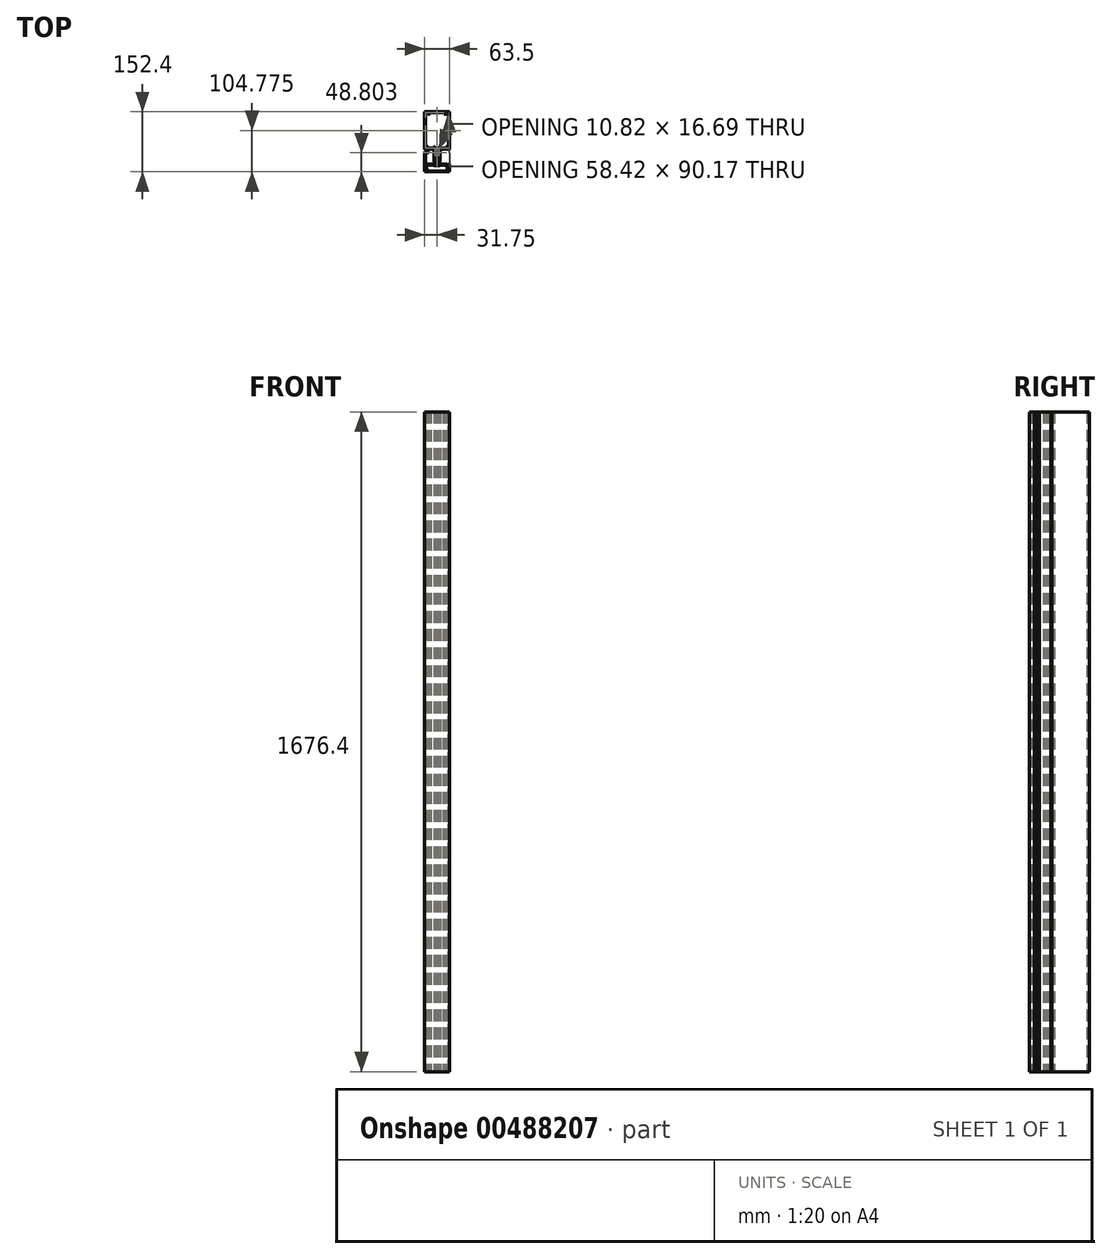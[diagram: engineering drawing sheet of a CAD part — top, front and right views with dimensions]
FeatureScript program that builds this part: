
annotation { "Feature Type Name" : "Feature", "Feature Type Description" : "" }
export const myFeature = defineFeature(function(context is Context, id is Id, definition is map)
    precondition{}
    {
        {
            var Q0;
            Q0=qCreatedBy(makeId("Top.planeOp"),FACE);
            var sketch = newSketch(context, id + "F0", { "sketchPlane" : qUnion([Q0])});
            skLineSegment(sketch, "E0", {"start": v(54.45, -82.55) * mm, "end": v(54.45, -2.69) * mm});
            skLineSegment(sketch, "E1", {"start": v(54.45, -2.69) * mm, "end": v(49.06, -1.35) * mm});
            skLineSegment(sketch, "E2", {"start": v(49.06, -1.35) * mm, "end": v(59.85, 1.35) * mm});
            skLineSegment(sketch, "E3", {"start": v(59.85, 1.35) * mm, "end": v(54.46, 2.69) * mm});
            skLineSegment(sketch, "E4", {"start": v(54.46, 2.69) * mm, "end": v(54.45, 82.55) * mm});
            skLineSegment(sketch, "E5", {"start": v(54.45, -31.75) * mm, "end": v(-9.05, -31.75) * mm});
            skLineSegment(sketch, "E6", {"start": v(-9.05, -44.45) * mm, "end": v(54.45, -44.45) * mm});
            skLineSegment(sketch, "E7", {"start": v(-2.7, -31.75) * mm, "end": v(-2.7, -44.45) * mm});
            skLineSegment(sketch, "E8", {"start": v(3.65, -76.2) * mm, "end": v(54.45, -76.2) * mm});
            skLineSegment(sketch, "E9", {"start": v(4.74, -64.5) * mm, "end": v(54.45, -64.5) * mm});
            skLineSegment(sketch, "E10", {"start": v(4.74, -11.7) * mm, "end": v(54.45, -11.7) * mm});
            skLineSegment(sketch, "E11", {"start": v(3.65, 76.2) * mm, "end": v(54.45, 76.2) * mm});
            skLineSegment(sketch, "E12", {"start": v(54.45, -25.4) * mm, "end": v(-9.05, -25.4) * mm});
            skLineSegment(sketch, "E13", {"start": v(-9.05, -25.4) * mm, "end": v(-9.05, -50.8) * mm});
            skLineSegment(sketch, "E14", {"start": v(-9.05, -50.8) * mm, "end": v(54.45, -50.8) * mm});
            skLineSegment(sketch, "E15", {"start": v(-24.72, -57.15) * mm, "end": v(-24.72, -60.33) * mm});
            skLineSegment(sketch, "E16", {"start": v(-31.48, -57.15) * mm, "end": v(-31.48, -60.33) * mm});
            skLineSegment(sketch, "E17", {"start": v(-50.7, -19.04) * mm, "end": v(-50.7, -25.4) * mm});
            skLineSegment(sketch, "E18", {"start": v(-59.84, -25.4) * mm, "end": v(-59.84, -19.04) * mm});
            skLineSegment(sketch, "E19", {"start": v(-36.05, -50.8) * mm, "end": v(-34.46, -50.8) * mm});
            skLineSegment(sketch, "E20", {"start": v(-36.05, -57.15) * mm, "end": v(-36.05, -50.8) * mm});
            skLineSegment(sketch, "E21", {"start": v(-20.15, -50.8) * mm, "end": v(-20.15, -57.15) * mm});
            skLineSegment(sketch, "E22", {"start": v(-21.74, -50.8) * mm, "end": v(-20.15, -50.8) * mm});
            skLineSegment(sketch, "E23", {"start": v(-36.05, -57.15) * mm, "end": v(-34.46, -57.15) * mm});
            skLineSegment(sketch, "E24", {"start": v(-21.74, -57.15) * mm, "end": v(-20.15, -57.15) * mm});
            skLineSegment(sketch, "E25", {"start": v(-34.45, -60.33) * mm, "end": v(-21.75, -60.33) * mm});
            skLineSegment(sketch, "E26", {"start": v(-58.58, -74.68) * mm, "end": v(-58.58, -65.43) * mm});
            skLineSegment(sketch, "E27", {"start": v(-58.58, -65.43) * mm, "end": v(-57.82, -65.43) * mm});
            skArc(sketch, "E28", {"start": v(-57.82, -65.43) * mm, "mid": v(-56.8, -64.41) * mm, "end": v(-57.82, -63.4) * mm});
            skLineSegment(sketch, "E29", {"start": v(-57.82, -63.4) * mm, "end": v(-58.33, -63.4) * mm});
            skArc(sketch, "E30", {"start": v(-58.33, -63.4) * mm, "mid": v(-59.4, -63.84) * mm, "end": v(-59.85, -64.92) * mm});
            skLineSegment(sketch, "E31", {"start": v(-59.85, -64.92) * mm, "end": v(-59.85, -76.2) * mm});
            skLineSegment(sketch, "E32", {"start": v(-59.85, -76.2) * mm, "end": v(3.65, -76.2) * mm});
            skLineSegment(sketch, "E33", {"start": v(3.65, -76.2) * mm, "end": v(3.65, -64.92) * mm});
            skArc(sketch, "E34", {"start": v(3.65, -64.92) * mm, "mid": v(3.2, -63.84) * mm, "end": v(2.13, -63.4) * mm});
            skLineSegment(sketch, "E35", {"start": v(2.13, -63.4) * mm, "end": v(1.62, -63.4) * mm});
            skArc(sketch, "E36", {"start": v(1.62, -63.4) * mm, "mid": v(0.6, -64.41) * mm, "end": v(1.62, -65.43) * mm});
            skLineSegment(sketch, "E37", {"start": v(1.62, -65.43) * mm, "end": v(2.38, -65.43) * mm});
            skLineSegment(sketch, "E38", {"start": v(2.38, -65.43) * mm, "end": v(2.38, -74.68) * mm});
            skLineSegment(sketch, "E39", {"start": v(2.38, -74.68) * mm, "end": v(-58.58, -74.68) * mm});
            skLineSegment(sketch, "E40", {"start": v(-8.53, -57.14) * mm, "end": v(-8.53, -50.8) * mm});
            skLineSegment(sketch, "E41", {"start": v(7.13, -50.8) * mm, "end": v(5.18, -64.5) * mm});
            skLineSegment(sketch, "E42", {"start": v(5.18, -64.5) * mm, "end": v(3.66, -64.5) * mm});
            skLineSegment(sketch, "E43", {"start": v(3.66, -64.5) * mm, "end": v(3.66, -61.57) * mm});
            skLineSegment(sketch, "E44", {"start": v(-8.53, -19.06) * mm, "end": v(-8.53, -25.4) * mm});
            skLineSegment(sketch, "E45", {"start": v(7.13, -25.4) * mm, "end": v(5.18, -11.7) * mm});
            skLineSegment(sketch, "E46", {"start": v(5.18, -11.7) * mm, "end": v(3.66, -11.7) * mm});
            skLineSegment(sketch, "E47", {"start": v(3.66, -11.7) * mm, "end": v(3.66, -14.63) * mm});
            skLineSegment(sketch, "E48", {"start": v(-33.5, -23.22) * mm, "end": v(-33.5, -34.99) * mm});
            skArc(sketch, "E49", {"start": v(-33.5, -34.99) * mm, "mid": v(-32.85, -35.74) * mm, "end": v(-32.01, -35.19) * mm});
            skLineSegment(sketch, "E50", {"start": v(-32.01, -35.19) * mm, "end": v(-31.6, -33.68) * mm});
            skArc(sketch, "E51", {"start": v(-31.6, -33.68) * mm, "mid": v(-28.1, -30.99) * mm, "end": v(-24.6, -33.68) * mm});
            skLineSegment(sketch, "E52", {"start": v(-24.6, -33.68) * mm, "end": v(-24.19, -35.19) * mm});
            skArc(sketch, "E53", {"start": v(-24.19, -35.19) * mm, "mid": v(-23.35, -35.74) * mm, "end": v(-22.69, -34.99) * mm});
            skLineSegment(sketch, "E54", {"start": v(-22.69, -34.99) * mm, "end": v(-22.69, -23.22) * mm});
            skArc(sketch, "E55", {"start": v(-22.69, -23.22) * mm, "mid": v(-23.8, -22.19) * mm, "end": v(-24.21, -20.73) * mm});
            skLineSegment(sketch, "E56", {"start": v(-24.21, -20.73) * mm, "end": v(-24.21, -19.05) * mm});
            skLineSegment(sketch, "E57", {"start": v(-24.21, -19.05) * mm, "end": v(-31.99, -19.05) * mm});
            skLineSegment(sketch, "E58", {"start": v(-31.99, -19.05) * mm, "end": v(-31.99, -20.73) * mm});
            skArc(sketch, "E59", {"start": v(-31.99, -20.73) * mm, "mid": v(-32.4, -22.19) * mm, "end": v(-33.5, -23.22) * mm});
            skLineSegment(sketch, "E60", {"start": v(-43.6, -19.05) * mm, "end": v(-34.78, -19.05) * mm});
            skArc(sketch, "E61", {"start": v(-34.78, -19.05) * mm, "mid": v(-34.6, -19.12) * mm, "end": v(-34.53, -19.3) * mm});
            skLineSegment(sketch, "E62", {"start": v(-34.53, -19.3) * mm, "end": v(-34.53, -20.73) * mm});
            skArc(sketch, "E63", {"start": v(-34.53, -20.73) * mm, "mid": v(-34.6, -20.9) * mm, "end": v(-34.78, -20.98) * mm});
            skLineSegment(sketch, "E64", {"start": v(-34.78, -20.98) * mm, "end": v(-35.8, -20.98) * mm});
            skArc(sketch, "E65", {"start": v(-35.8, -20.98) * mm, "mid": v(-35.98, -21.05) * mm, "end": v(-36.05, -21.23) * mm});
            skLineSegment(sketch, "E66", {"start": v(-36.05, -21.23) * mm, "end": v(-36.05, -50.8) * mm});
            skLineSegment(sketch, "E67", {"start": v(-36.05, -50.8) * mm, "end": v(-35.03, -50.8) * mm});
            skLineSegment(sketch, "E68", {"start": v(-35.03, -50.8) * mm, "end": v(-34.65, -51.18) * mm});
            skLineSegment(sketch, "E69", {"start": v(-34.65, -51.18) * mm, "end": v(-34.27, -50.8) * mm});
            skLineSegment(sketch, "E70", {"start": v(-34.27, -50.8) * mm, "end": v(-32.42, -50.8) * mm});
            skLineSegment(sketch, "E71", {"start": v(-32.42, -50.8) * mm, "end": v(-32.04, -51.18) * mm});
            skLineSegment(sketch, "E72", {"start": v(-32.04, -51.18) * mm, "end": v(-31.66, -50.8) * mm});
            skLineSegment(sketch, "E73", {"start": v(-31.66, -50.8) * mm, "end": v(-30.64, -50.8) * mm});
            skLineSegment(sketch, "E74", {"start": v(-30.64, -50.8) * mm, "end": v(-30.64, -39.88) * mm});
            skLineSegment(sketch, "E75", {"start": v(-30.64, -39.88) * mm, "end": v(-29.16, -34.34) * mm});
            skArc(sketch, "E76", {"start": v(-29.16, -34.34) * mm, "mid": v(-28.1, -33.53) * mm, "end": v(-27.04, -34.34) * mm});
            skLineSegment(sketch, "E77", {"start": v(-27.04, -34.34) * mm, "end": v(-25.56, -39.88) * mm});
            skLineSegment(sketch, "E78", {"start": v(-25.56, -39.88) * mm, "end": v(-25.56, -50.8) * mm});
            skLineSegment(sketch, "E79", {"start": v(-25.56, -50.8) * mm, "end": v(-24.54, -50.8) * mm});
            skLineSegment(sketch, "E80", {"start": v(-24.54, -50.8) * mm, "end": v(-24.16, -51.18) * mm});
            skLineSegment(sketch, "E81", {"start": v(-24.16, -51.18) * mm, "end": v(-23.78, -50.8) * mm});
            skLineSegment(sketch, "E82", {"start": v(-23.78, -50.8) * mm, "end": v(-21.93, -50.8) * mm});
            skLineSegment(sketch, "E83", {"start": v(-21.93, -50.8) * mm, "end": v(-21.55, -51.18) * mm});
            skLineSegment(sketch, "E84", {"start": v(-21.55, -51.18) * mm, "end": v(-21.17, -50.8) * mm});
            skLineSegment(sketch, "E85", {"start": v(-21.17, -50.8) * mm, "end": v(-20.15, -50.8) * mm});
            skLineSegment(sketch, "E86", {"start": v(-20.15, -50.8) * mm, "end": v(-20.15, -21.23) * mm});
            skArc(sketch, "E87", {"start": v(-20.15, -21.23) * mm, "mid": v(-20.22, -21.05) * mm, "end": v(-20.4, -20.98) * mm});
            skLineSegment(sketch, "E88", {"start": v(-20.4, -20.98) * mm, "end": v(-21.42, -20.98) * mm});
            skArc(sketch, "E89", {"start": v(-21.42, -20.98) * mm, "mid": v(-21.6, -20.9) * mm, "end": v(-21.67, -20.73) * mm});
            skLineSegment(sketch, "E90", {"start": v(-21.67, -20.73) * mm, "end": v(-21.67, -19.3) * mm});
            skArc(sketch, "E91", {"start": v(-21.67, -19.3) * mm, "mid": v(-21.6, -19.12) * mm, "end": v(-21.42, -19.05) * mm});
            skLineSegment(sketch, "E92", {"start": v(-21.42, -19.05) * mm, "end": v(-12.6, -19.05) * mm});
            skLineSegment(sketch, "E93", {"start": v(-12.6, -19.05) * mm, "end": v(-12.22, -18.67) * mm});
            skLineSegment(sketch, "E94", {"start": v(-12.22, -18.67) * mm, "end": v(-11.84, -19.05) * mm});
            skLineSegment(sketch, "E95", {"start": v(-11.84, -19.05) * mm, "end": v(-2.9, -19.05) * mm});
            skArc(sketch, "E96", {"start": v(-2.9, -19.05) * mm, "mid": v(-2.55, -18.81) * mm, "end": v(-2.63, -18.4) * mm});
            skArc(sketch, "E97", {"start": v(-2.63, -18.4) * mm, "mid": v(-3.13, -17.66) * mm, "end": v(-3.3, -16.78) * mm});
            skLineSegment(sketch, "E98", {"start": v(-3.3, -16.78) * mm, "end": v(-3.3, -16.51) * mm});
            skArc(sketch, "E99", {"start": v(-3.3, -16.51) * mm, "mid": v(-2.94, -15.61) * mm, "end": v(-2.04, -15.24) * mm});
            skLineSegment(sketch, "E100", {"start": v(-2.04, -15.24) * mm, "end": v(0.2, -15.24) * mm});
            skArc(sketch, "E101", {"start": v(0.2, -15.24) * mm, "mid": v(1.1, -15.61) * mm, "end": v(1.47, -16.51) * mm});
            skLineSegment(sketch, "E102", {"start": v(1.47, -16.51) * mm, "end": v(1.47, -16.78) * mm});
            skArc(sketch, "E103", {"start": v(1.47, -16.78) * mm, "mid": v(1.3, -17.66) * mm, "end": v(0.8, -18.4) * mm});
            skArc(sketch, "E104", {"start": v(0.8, -18.4) * mm, "mid": v(0.7, -18.81) * mm, "end": v(1.06, -19.05) * mm});
            skLineSegment(sketch, "E105", {"start": v(1.06, -19.05) * mm, "end": v(3.14, -19.05) * mm});
            skArc(sketch, "E106", {"start": v(3.14, -19.05) * mm, "mid": v(3.5, -18.9) * mm, "end": v(3.65, -18.54) * mm});
            skLineSegment(sketch, "E107", {"start": v(3.65, -18.54) * mm, "end": v(3.65, 76.2) * mm});
            skLineSegment(sketch, "E108", {"start": v(3.65, 76.2) * mm, "end": v(-59.85, 76.2) * mm});
            skLineSegment(sketch, "E109", {"start": v(-59.85, 76.2) * mm, "end": v(-59.85, -18.54) * mm});
            skArc(sketch, "E110", {"start": v(-59.85, -18.54) * mm, "mid": v(-59.7, -18.9) * mm, "end": v(-59.34, -19.05) * mm});
            skLineSegment(sketch, "E111", {"start": v(-59.34, -19.05) * mm, "end": v(-57.26, -19.05) * mm});
            skArc(sketch, "E112", {"start": v(-57.26, -19.05) * mm, "mid": v(-56.9, -18.81) * mm, "end": v(-57, -18.4) * mm});
            skArc(sketch, "E113", {"start": v(-57, -18.4) * mm, "mid": v(-57.49, -17.66) * mm, "end": v(-57.67, -16.78) * mm});
            skLineSegment(sketch, "E114", {"start": v(-57.67, -16.78) * mm, "end": v(-57.67, -16.51) * mm});
            skArc(sketch, "E115", {"start": v(-57.67, -16.51) * mm, "mid": v(-57.3, -15.61) * mm, "end": v(-56.4, -15.24) * mm});
            skLineSegment(sketch, "E116", {"start": v(-56.4, -15.24) * mm, "end": v(-54.16, -15.24) * mm});
            skArc(sketch, "E117", {"start": v(-54.16, -15.24) * mm, "mid": v(-53.26, -15.61) * mm, "end": v(-52.9, -16.51) * mm});
            skLineSegment(sketch, "E118", {"start": v(-52.9, -16.51) * mm, "end": v(-52.9, -16.78) * mm});
            skArc(sketch, "E119", {"start": v(-52.9, -16.78) * mm, "mid": v(-53.07, -17.66) * mm, "end": v(-53.56, -18.4) * mm});
            skArc(sketch, "E120", {"start": v(-53.56, -18.4) * mm, "mid": v(-53.65, -18.81) * mm, "end": v(-53.3, -19.05) * mm});
            skLineSegment(sketch, "E121", {"start": v(-53.3, -19.05) * mm, "end": v(-44.36, -19.05) * mm});
            skLineSegment(sketch, "E122", {"start": v(-44.36, -19.05) * mm, "end": v(-43.97, -18.67) * mm});
            skLineSegment(sketch, "E123", {"start": v(-43.97, -18.67) * mm, "end": v(-43.6, -19.05) * mm});
            skArc(sketch, "E124", {"start": v(-34.02, -13.2) * mm, "mid": v(-34.17, -12.85) * mm, "end": v(-34.53, -12.7) * mm});
            skLineSegment(sketch, "E125", {"start": v(-34.53, -12.7) * mm, "end": v(-35.54, -12.7) * mm});
            skArc(sketch, "E126", {"start": v(-35.54, -12.7) * mm, "mid": v(-35.9, -12.85) * mm, "end": v(-36.05, -13.2) * mm});
            skLineSegment(sketch, "E127", {"start": v(-36.05, -13.2) * mm, "end": v(-36.05, -15.88) * mm});
            skLineSegment(sketch, "E128", {"start": v(-36.05, -15.88) * mm, "end": v(-50.83, -15.88) * mm});
            skLineSegment(sketch, "E129", {"start": v(-50.83, -15.88) * mm, "end": v(-50.83, -13.2) * mm});
            skArc(sketch, "E130", {"start": v(-50.83, -13.2) * mm, "mid": v(-50.98, -12.85) * mm, "end": v(-51.34, -12.7) * mm});
            skLineSegment(sketch, "E131", {"start": v(-51.34, -12.7) * mm, "end": v(-56.55, -12.7) * mm});
            skArc(sketch, "E132", {"start": v(-56.55, -12.7) * mm, "mid": v(-57.09, -12.48) * mm, "end": v(-57.3, -11.94) * mm});
            skLineSegment(sketch, "E133", {"start": v(-57.3, -11.94) * mm, "end": v(-57.3, 73.66) * mm});
            skLineSegment(sketch, "E134", {"start": v(-57.3, 73.66) * mm, "end": v(-53.25, 73.66) * mm});
            skArc(sketch, "E135", {"start": v(-53.25, 73.66) * mm, "mid": v(-52.17, 73.21) * mm, "end": v(-51.72, 72.14) * mm});
            skLineSegment(sketch, "E136", {"start": v(-51.72, 72.14) * mm, "end": v(-51.72, 70.61) * mm});
            skLineSegment(sketch, "E137", {"start": v(-51.72, 70.61) * mm, "end": v(-45.75, 70.61) * mm});
            skLineSegment(sketch, "E138", {"start": v(-45.75, 70.61) * mm, "end": v(-45.75, 72.14) * mm});
            skArc(sketch, "E139", {"start": v(-45.75, 72.14) * mm, "mid": v(-45.3, 73.21) * mm, "end": v(-44.23, 73.66) * mm});
            skLineSegment(sketch, "E140", {"start": v(-44.23, 73.66) * mm, "end": v(-11.97, 73.66) * mm});
            skArc(sketch, "E141", {"start": v(-11.97, 73.66) * mm, "mid": v(-10.9, 73.21) * mm, "end": v(-10.45, 72.14) * mm});
            skLineSegment(sketch, "E142", {"start": v(-10.45, 72.14) * mm, "end": v(-10.45, 70.61) * mm});
            skLineSegment(sketch, "E143", {"start": v(-10.45, 70.61) * mm, "end": v(-4.48, 70.61) * mm});
            skLineSegment(sketch, "E144", {"start": v(-4.48, 70.61) * mm, "end": v(-4.48, 72.14) * mm});
            skArc(sketch, "E145", {"start": v(-4.48, 72.14) * mm, "mid": v(-4.03, 73.21) * mm, "end": v(-2.95, 73.66) * mm});
            skLineSegment(sketch, "E146", {"start": v(-2.95, 73.66) * mm, "end": v(1.11, 73.66) * mm});
            skLineSegment(sketch, "E147", {"start": v(1.11, 73.66) * mm, "end": v(1.11, -11.94) * mm});
            skArc(sketch, "E148", {"start": v(1.11, -11.94) * mm, "mid": v(0.89, -12.48) * mm, "end": v(0.35, -12.7) * mm});
            skLineSegment(sketch, "E149", {"start": v(0.35, -12.7) * mm, "end": v(-4.86, -12.7) * mm});
            skArc(sketch, "E150", {"start": v(-4.86, -12.7) * mm, "mid": v(-5.22, -12.85) * mm, "end": v(-5.37, -13.2) * mm});
            skLineSegment(sketch, "E151", {"start": v(-5.37, -13.2) * mm, "end": v(-5.37, -15.88) * mm});
            skLineSegment(sketch, "E152", {"start": v(-5.37, -15.88) * mm, "end": v(-20.15, -15.88) * mm});
            skLineSegment(sketch, "E153", {"start": v(-20.15, -15.88) * mm, "end": v(-20.15, -13.2) * mm});
            skArc(sketch, "E154", {"start": v(-20.15, -13.2) * mm, "mid": v(-20.3, -12.85) * mm, "end": v(-20.66, -12.7) * mm});
            skLineSegment(sketch, "E155", {"start": v(-20.66, -12.7) * mm, "end": v(-21.67, -12.7) * mm});
            skArc(sketch, "E156", {"start": v(-21.67, -12.7) * mm, "mid": v(-22.03, -12.85) * mm, "end": v(-22.18, -13.2) * mm});
            skLineSegment(sketch, "E157", {"start": v(-22.18, -13.2) * mm, "end": v(-22.18, -16.51) * mm});
            skLineSegment(sketch, "E158", {"start": v(-22.18, -16.51) * mm, "end": v(-34.02, -16.51) * mm});
            skLineSegment(sketch, "E159", {"start": v(-34.02, -16.51) * mm, "end": v(-34.02, -13.2) * mm});
            skLineSegment(sketch, "E160", {"start": v(-5.85, -59.69) * mm, "end": v(-19.84, -59.69) * mm});
            skLineSegment(sketch, "E161", {"start": v(-19.84, -59.69) * mm, "end": v(-20.48, -60.33) * mm});
            skLineSegment(sketch, "E162", {"start": v(-20.48, -60.33) * mm, "end": v(-27.72, -60.33) * mm});
            skLineSegment(sketch, "E163", {"start": v(-27.72, -60.33) * mm, "end": v(-28.1, -59.94) * mm});
            skLineSegment(sketch, "E164", {"start": v(-28.1, -59.94) * mm, "end": v(-28.48, -60.33) * mm});
            skLineSegment(sketch, "E165", {"start": v(-28.48, -60.33) * mm, "end": v(-35.72, -60.33) * mm});
            skLineSegment(sketch, "E166", {"start": v(-35.72, -60.33) * mm, "end": v(-36.35, -59.69) * mm});
            skLineSegment(sketch, "E167", {"start": v(-36.35, -59.69) * mm, "end": v(-54.77, -59.69) * mm});
            skLineSegment(sketch, "E168", {"start": v(-54.77, -59.69) * mm, "end": v(-54.77, -66.57) * mm});
            skLineSegment(sketch, "E169", {"start": v(-54.77, -66.57) * mm, "end": v(-53.23, -69.24) * mm});
            skArc(sketch, "E170", {"start": v(-53.23, -69.24) * mm, "mid": v(-53.6, -70.63) * mm, "end": v(-54.99, -70.26) * mm});
            skLineSegment(sketch, "E171", {"start": v(-54.99, -70.26) * mm, "end": v(-57.67, -65.62) * mm});
            skArc(sketch, "E172", {"start": v(-57.67, -65.62) * mm, "mid": v(-56.82, -64.2) * mm, "end": v(-58.07, -63.14) * mm});
            skLineSegment(sketch, "E173", {"start": v(-58.07, -63.14) * mm, "end": v(-59.09, -63.14) * mm});
            skArc(sketch, "E174", {"start": v(-59.09, -63.14) * mm, "mid": v(-59.63, -62.92) * mm, "end": v(-59.85, -62.38) * mm});
            skLineSegment(sketch, "E175", {"start": v(-59.85, -62.38) * mm, "end": v(-59.85, -25.4) * mm});
            skLineSegment(sketch, "E176", {"start": v(-59.85, -25.4) * mm, "end": v(-50.45, -25.4) * mm});
            skArc(sketch, "E177", {"start": v(-50.45, -25.4) * mm, "mid": v(-49.91, -25.62) * mm, "end": v(-49.69, -26.16) * mm});
            skLineSegment(sketch, "E178", {"start": v(-49.69, -26.16) * mm, "end": v(-49.69, -27.18) * mm});
            skArc(sketch, "E179", {"start": v(-49.69, -27.18) * mm, "mid": v(-49.91, -27.72) * mm, "end": v(-50.45, -27.94) * mm});
            skLineSegment(sketch, "E180", {"start": v(-50.45, -27.94) * mm, "end": v(-55.79, -27.94) * mm});
            skArc(sketch, "E181", {"start": v(-55.79, -27.94) * mm, "mid": v(-56.86, -28.39) * mm, "end": v(-57.3, -29.46) * mm});
            skLineSegment(sketch, "E182", {"start": v(-57.3, -29.46) * mm, "end": v(-57.3, -55.63) * mm});
            skArc(sketch, "E183", {"start": v(-57.3, -55.63) * mm, "mid": v(-56.86, -56.7) * mm, "end": v(-55.79, -57.15) * mm});
            skLineSegment(sketch, "E184", {"start": v(-55.79, -57.15) * mm, "end": v(-33.81, -57.15) * mm});
            skLineSegment(sketch, "E185", {"start": v(-33.81, -57.15) * mm, "end": v(-33.43, -56.77) * mm});
            skLineSegment(sketch, "E186", {"start": v(-33.43, -56.77) * mm, "end": v(-33.05, -57.15) * mm});
            skLineSegment(sketch, "E187", {"start": v(-33.05, -57.15) * mm, "end": v(-23.15, -57.15) * mm});
            skLineSegment(sketch, "E188", {"start": v(-23.15, -57.15) * mm, "end": v(-22.77, -56.77) * mm});
            skLineSegment(sketch, "E189", {"start": v(-22.77, -56.77) * mm, "end": v(-22.38, -57.15) * mm});
            skLineSegment(sketch, "E190", {"start": v(-22.38, -57.15) * mm, "end": v(-2.9, -57.15) * mm});
            skArc(sketch, "E191", {"start": v(-2.9, -57.15) * mm, "mid": v(-2.55, -57.39) * mm, "end": v(-2.63, -57.8) * mm});
            skArc(sketch, "E192", {"start": v(-2.63, -57.8) * mm, "mid": v(-3.13, -58.54) * mm, "end": v(-3.3, -59.42) * mm});
            skLineSegment(sketch, "E193", {"start": v(-3.3, -59.42) * mm, "end": v(-3.3, -59.69) * mm});
            skArc(sketch, "E194", {"start": v(-3.3, -59.69) * mm, "mid": v(-2.94, -60.59) * mm, "end": v(-2.04, -60.96) * mm});
            skLineSegment(sketch, "E195", {"start": v(-2.04, -60.96) * mm, "end": v(0.2, -60.96) * mm});
            skArc(sketch, "E196", {"start": v(0.2, -60.96) * mm, "mid": v(1.1, -60.59) * mm, "end": v(1.47, -59.69) * mm});
            skLineSegment(sketch, "E197", {"start": v(1.47, -59.69) * mm, "end": v(1.47, -59.42) * mm});
            skArc(sketch, "E198", {"start": v(1.47, -59.42) * mm, "mid": v(1.3, -58.54) * mm, "end": v(0.8, -57.8) * mm});
            skArc(sketch, "E199", {"start": v(0.8, -57.8) * mm, "mid": v(0.7, -57.39) * mm, "end": v(1.06, -57.15) * mm});
            skLineSegment(sketch, "E200", {"start": v(1.06, -57.15) * mm, "end": v(3.14, -57.15) * mm});
            skArc(sketch, "E201", {"start": v(3.14, -57.15) * mm, "mid": v(3.5, -57.3) * mm, "end": v(3.65, -57.66) * mm});
            skLineSegment(sketch, "E202", {"start": v(3.65, -57.66) * mm, "end": v(3.65, -62.38) * mm});
            skArc(sketch, "E203", {"start": v(3.65, -62.38) * mm, "mid": v(3.43, -62.92) * mm, "end": v(2.89, -63.14) * mm});
            skLineSegment(sketch, "E204", {"start": v(2.89, -63.14) * mm, "end": v(1.87, -63.14) * mm});
            skArc(sketch, "E205", {"start": v(1.87, -63.14) * mm, "mid": v(0.62, -64.2) * mm, "end": v(1.47, -65.62) * mm});
            skLineSegment(sketch, "E206", {"start": v(1.47, -65.62) * mm, "end": v(-1.21, -70.26) * mm});
            skArc(sketch, "E207", {"start": v(-1.21, -70.26) * mm, "mid": v(-2.6, -70.63) * mm, "end": v(-2.97, -69.24) * mm});
            skLineSegment(sketch, "E208", {"start": v(-2.97, -69.24) * mm, "end": v(-1.43, -66.57) * mm});
            skLineSegment(sketch, "E209", {"start": v(-1.43, -66.57) * mm, "end": v(-1.43, -63.14) * mm});
            skLineSegment(sketch, "E210", {"start": v(-1.43, -63.14) * mm, "end": v(-4.33, -63.14) * mm});
            skArc(sketch, "E211", {"start": v(-4.33, -63.14) * mm, "mid": v(-5.4, -62.7) * mm, "end": v(-5.85, -61.62) * mm});
            skLineSegment(sketch, "E212", {"start": v(-5.85, -61.62) * mm, "end": v(-5.85, -59.69) * mm});
            skSolve(sketch);
        }
        {
            var Q0;
            Q0=makeQuery(id+"F0.imprint","IMPRINT",FACE,{"disambiguationData":[TD([[makeQuery(id+"F0.imprint","IMPRINT",EDGE,{"derivedFrom":sQuery(id+"F0.wireOp",EDGE,"E48")}),-1.0]])]});
            extrude(context, id + "F1", {"entities" : qUnion([Q0]), "endBound" : BoundingType.SYMMETRIC, "depth" : 1676.4 * mm});
        }
        {
            var Q0;
            {var subQ7=sQuery(id+"F0.wireOp",EDGE,"E16");Q0=makeQuery(id+"F0.imprint","IMPRINT",FACE,{"disambiguationData":[TD([[makeQuery(id+"F0.imprint","IMPRINT",EDGE,{"derivedFrom":subQ7}),-1.0]])]});}
            var Q1;
            {var subQ0=sQuery(id+"F0.wireOp",EDGE,"E15");Q1=makeQuery(id+"F0.imprint","IMPRINT",FACE,{"disambiguationData":[TD([[makeQuery(id+"F0.imprint","IMPRINT",EDGE,{"derivedFrom":subQ0}),1.0]])]});}
            var Q2;
            Q2=makeQuery(id+"F0.imprint","IMPRINT",FACE,{"disambiguationData":[TD([[makeQuery(id+"F0.imprint","IMPRINT",EDGE,{"derivedFrom":sQuery(id+"F0.wireOp",EDGE,"E26")}),1.0]])]});
            extrude(context, id + "F2", {"entities" : qUnion([Q0, Q1, Q2]), "endBound" : BoundingType.SYMMETRIC, "depth" : 1676.4 * mm});
        }
        {
            var Q0;
            {var subQ3=sQuery(id+"F0.wireOp",EDGE,"E15");Q0=makeQuery(id+"F0.imprint","IMPRINT",FACE,{"disambiguationData":[TD([[makeQuery(id+"F0.imprint","IMPRINT",EDGE,{"derivedFrom":subQ3}),-1.0]])]});}
            extrude(context, id + "F3", {"entities" : qUnion([Q0]), "endBound" : BoundingType.SYMMETRIC, "depth" : 1676.4 * mm});
        }
    });
